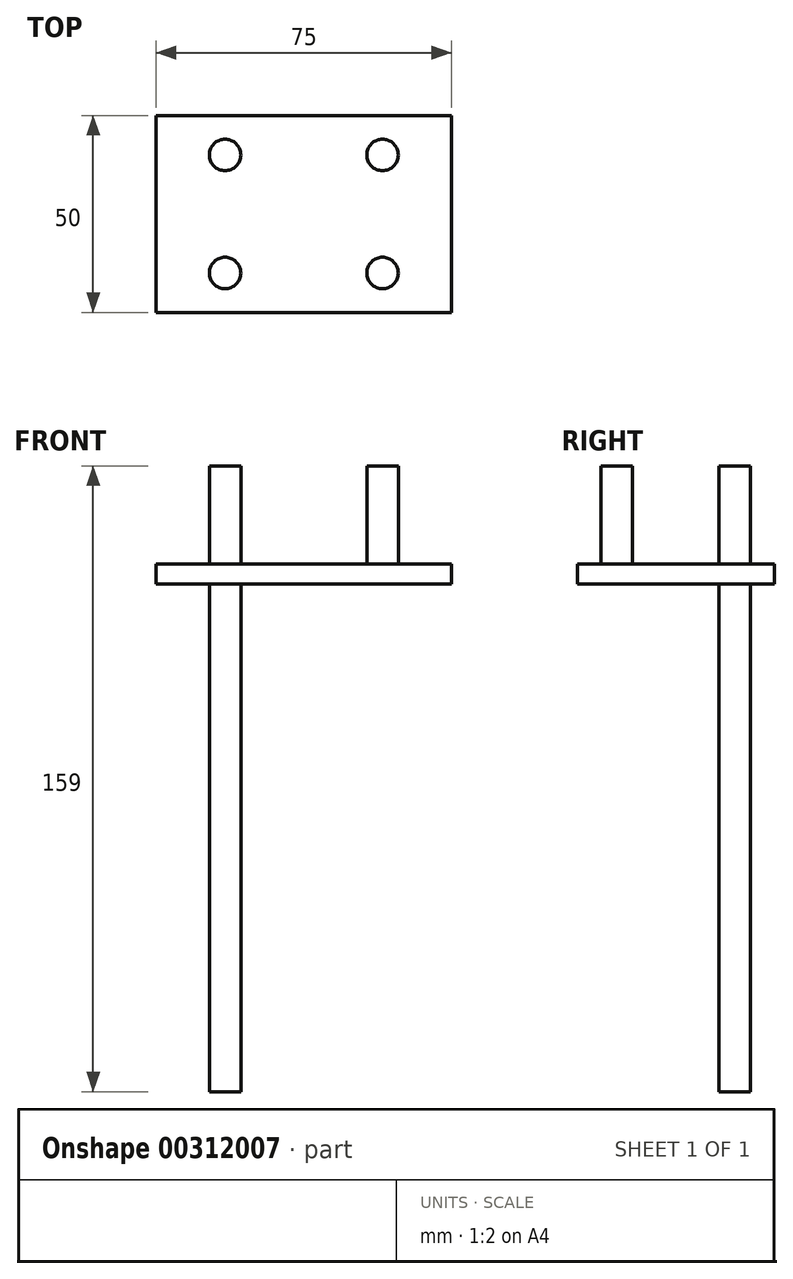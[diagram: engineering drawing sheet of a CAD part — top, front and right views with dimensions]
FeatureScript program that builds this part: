
annotation { "Feature Type Name" : "Feature", "Feature Type Description" : "" }
export const myFeature = defineFeature(function(context is Context, id is Id, definition is map)
    precondition{}
    {
        {
            var Q0;
            Q0=qCreatedBy(makeId("Top.planeOp"),FACE);
            var sketch = newSketch(context, id + "F0", { "sketchPlane" : qUnion([Q0])});
            skLineSegment(sketch, "E0.rect.bottom", {"start": v(37.5, 25) * mm, "end": v(-37.5, 25) * mm});
            skLineSegment(sketch, "E0.rect.top", {"start": v(37.5, -25) * mm, "end": v(-37.5, -25) * mm});
            skLineSegment(sketch, "E0.rect.left", {"start": v(37.5, 25) * mm, "end": v(37.5, -25) * mm});
            skLineSegment(sketch, "E0.rect.right", {"start": v(-37.5, 25) * mm, "end": v(-37.5, -25) * mm});
            skPoint(sketch, "E0.rect.middle", {"position": v(0, 0) * mm});
            skSolve(sketch);
        }
        {
            var Q0;
            Q0=qSketchRegion(id+"F0",true);
            extrude(context, id + "F1", {"entities" : qUnion([Q0]), "depth" : 5 * mm});
        }
        {
            var Q0;
            Q0=makeQuery(id+"F1.opExtrude","CAP_FACE",FACE,{"disambiguationData":[OSD([sQuery(id+"F0.wireOp",EDGE,"E0.rect.bottom"),sQuery(id+"F0.wireOp",EDGE,"E0.rect.top"),sQuery(id+"F0.wireOp",EDGE,"E0.rect.left"),sQuery(id+"F0.wireOp",EDGE,"E0.rect.right")])],"isStart":false});
            var sketch = newSketch(context, id + "F2", { "sketchPlane" : qUnion([Q0])});
            skLineSegment(sketch, "E1", {"start": v(16, 15) * mm, "end": v(20, 15) * mm});
            skLineSegment(sketch, "E2", {"start": v(20, 15) * mm, "end": v(20, 11) * mm});
            skLineSegment(sketch, "E3.0.MirrorCS", {"start": v(16, -15) * mm, "end": v(20, -15) * mm});
            skLineSegment(sketch, "E4.0.MirrorCS", {"start": v(20, -15) * mm, "end": v(20, -11) * mm});
            skCircle(sketch, "E5", {"center": v(-20, 15) * mm, "radius": 4 * mm});
            skCircle(sketch, "E6.0.MirrorC", {"center": v(20, 15) * mm, "radius": 4 * mm});
            skCircle(sketch, "E7.0.MirrorC", {"center": v(-20, -15) * mm, "radius": 4 * mm});
            skCircle(sketch, "E8.0.MirrorC", {"center": v(20, -15) * mm, "radius": 4 * mm});
            skPoint(sketch, "E9.orphan", {"position": v(0, 15) * mm});
            skPoint(sketch, "E10.orphan", {"position": v(-20, 0) * mm});
            skPoint(sketch, "E11.trimOffspring.end.orphan", {"position": v(0, -25) * mm});
            skPoint(sketch, "E12.start.orphan", {"position": v(0, 25) * mm});
            skPoint(sketch, "E13.0.MirrorCS.start.orphan", {"position": v(37.5, 0) * mm});
            skPoint(sketch, "E14.end.orphan", {"position": v(-37.5, 0) * mm});
            skSolve(sketch);
        }
        {
            var Q0;
            Q0=qSketchRegion(id+"F2",true);
            extrude(context, id + "F3", {"entities" : qUnion([Q0]), "operationType" : NewBodyOperationType.ADD, "depth" : 25 * mm});
        }
        {
            var Q0;
            Q0=makeQuery(id+"F3.opExtrude","CAP_FACE",FACE,{"disambiguationData":[OSD([sQuery(id+"F2.wireOp",EDGE,"E5")])],"isStart":false});
            extrude(context, id + "F4", {"entities" : qUnion([Q0]), "operationType" : NewBodyOperationType.ADD, "oppositeDirection" : true, "depth" : 159 * mm});
        }
    });
